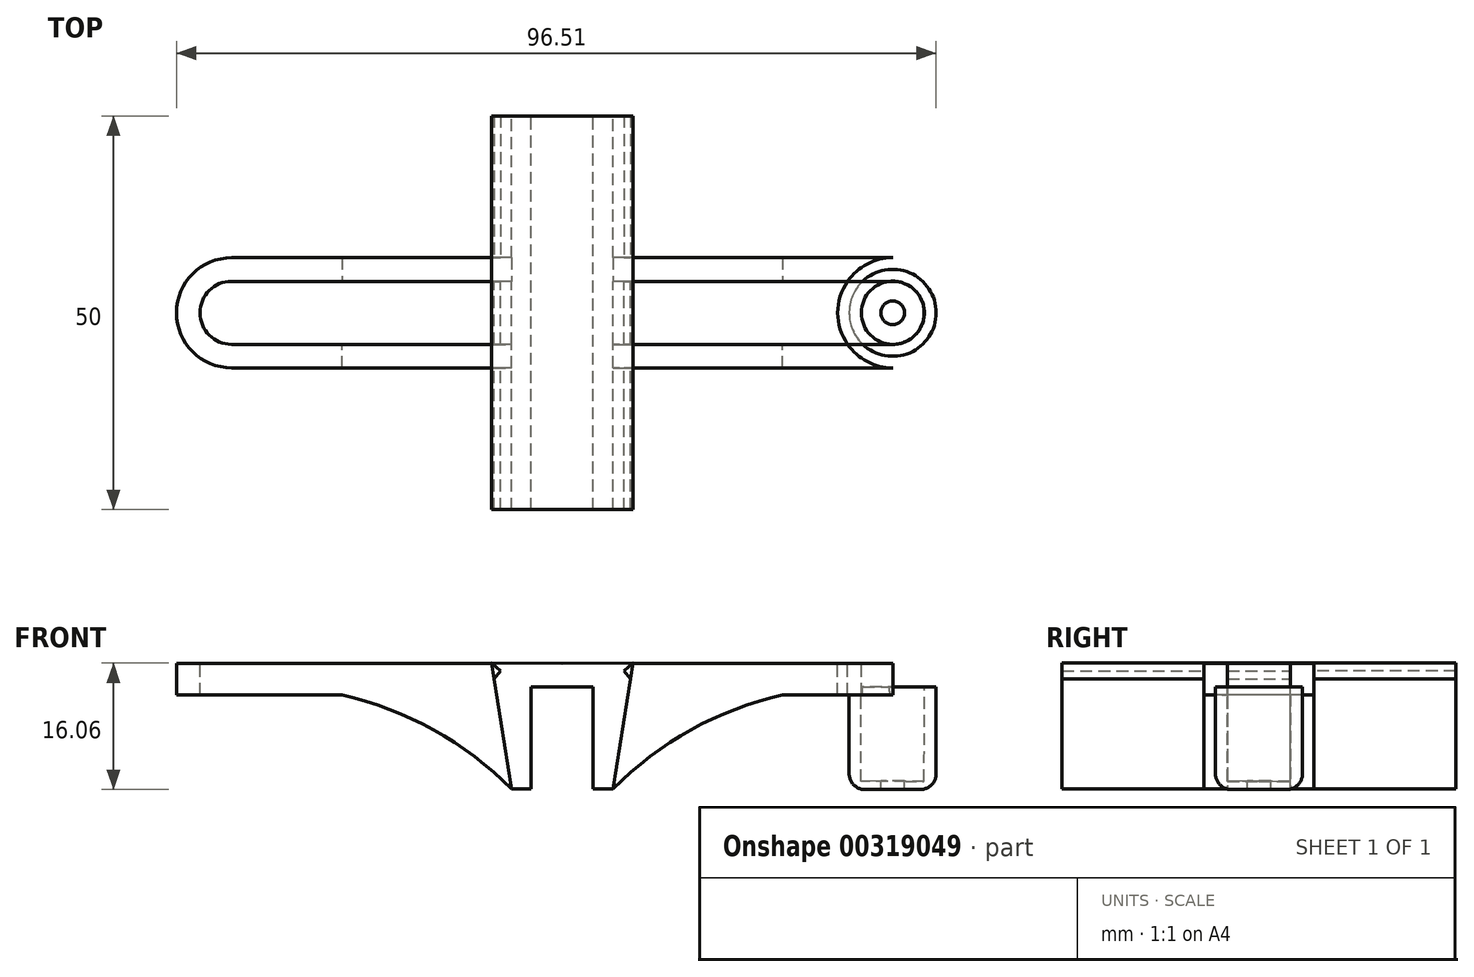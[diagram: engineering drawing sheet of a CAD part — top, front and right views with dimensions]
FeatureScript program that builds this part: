
annotation { "Feature Type Name" : "Feature", "Feature Type Description" : "" }
export const myFeature = defineFeature(function(context is Context, id is Id, definition is map)
    precondition{}
    {
        {
            var Q0;
            Q0=qCreatedBy(makeId("Front.planeOp"),FACE);
            var sketch = newSketch(context, id + "F0", { "sketchPlane" : qUnion([Q0])});
            skLineSegment(sketch, "E0", {"start": v(6.45, -15.97) * mm, "end": v(3.95, -15.97) * mm});
            skLineSegment(sketch, "E1", {"start": v(3.95, -15.97) * mm, "end": v(3.95, -2.97) * mm});
            skLineSegment(sketch, "E2", {"start": v(0, 0) * mm, "end": v(0, -15.97) * mm, "construction": true});
            skLineSegment(sketch, "E3", {"start": v(9, 0.03) * mm, "end": v(49, 0.03) * mm});
            skLineSegment(sketch, "E4", {"start": v(49, 0.03) * mm, "end": v(49, -2.97) * mm});
            skLineSegment(sketch, "E5", {"start": v(49, -2.97) * mm, "end": v(8.52, -2.97) * mm});
            skLineSegment(sketch, "E6", {"start": v(49, 0.03) * mm, "end": v(46, 0.03) * mm, "construction": true});
            skLineSegment(sketch, "E7", {"start": v(46, 0.03) * mm, "end": v(46, -2.97) * mm});
            skLineSegment(sketch, "E8", {"start": v(0, 0) * mm, "end": v(0, -2.97) * mm});
            skLineSegment(sketch, "E9", {"start": v(9, 0.03) * mm, "end": v(0, 0) * mm});
            skLineSegment(sketch, "E10", {"start": v(0, -2.97) * mm, "end": v(3.95, -2.97) * mm});
            skLineSegment(sketch, "E11", {"start": v(8.52, -2.97) * mm, "end": v(49, -2.97) * mm});
            skLineSegment(sketch, "E12.MirrorCS", {"start": v(0, -2.97) * mm, "end": v(-3.95, -2.97) * mm});
            skLineSegment(sketch, "E13.MirrorCS", {"start": v(-9, 0.03) * mm, "end": v(0, 0) * mm});
            skLineSegment(sketch, "E14.MirrorCS", {"start": v(-3.95, -15.97) * mm, "end": v(-3.95, -2.97) * mm});
            skLineSegment(sketch, "E15.MirrorCS", {"start": v(-6.45, -15.97) * mm, "end": v(-3.95, -15.97) * mm});
            skLineSegment(sketch, "E16.MirrorCS", {"start": v(-9, 0.03) * mm, "end": v(-49, 0.03) * mm});
            skLineSegment(sketch, "E17.MirrorCS", {"start": v(-49, 0.03) * mm, "end": v(-49, -2.97) * mm});
            skLineSegment(sketch, "E18.MirrorCS", {"start": v(-49, -2.97) * mm, "end": v(-8.52, -2.97) * mm});
            skLineSegment(sketch, "E19.MirrorCS", {"start": v(-46, 0.03) * mm, "end": v(-46, -2.97) * mm});
            skLineSegment(sketch, "E20", {"start": v(38, 0.03) * mm, "end": v(38, -2.97) * mm});
            skLineSegment(sketch, "E21", {"start": v(35, 0.03) * mm, "end": v(35, -2.97) * mm});
            skLineSegment(sketch, "E22", {"start": v(45.98, -14.97) * mm, "end": v(46, -2.97) * mm});
            skLineSegment(sketch, "E23", {"start": v(36.5, -2.97) * mm, "end": v(36.5, -16.03) * mm});
            skLineSegment(sketch, "E24", {"start": v(36.5, -16.03) * mm, "end": v(47.5, -16.03) * mm});
            skLineSegment(sketch, "E25", {"start": v(47.5, -16.03) * mm, "end": v(47.5, -2.97) * mm});
            skLineSegment(sketch, "E26", {"start": v(45.98, -14.97) * mm, "end": v(37.98, -14.96) * mm});
            skLineSegment(sketch, "E27", {"start": v(37.98, -14.96) * mm, "end": v(38, -2.97) * mm});
            skLineSegment(sketch, "E28", {"start": v(41.98, 0) * mm, "end": v(41.98, -16.03) * mm, "construction": true});
            skPoint(sketch, "E28.startSnap0", {"position": v(41.98, -14.96) * mm});
            skLineSegment(sketch, "E29", {"start": v(43.48, -14.97) * mm, "end": v(43.48, -16.03) * mm});
            skLineSegment(sketch, "E30", {"start": v(40.48, -14.96) * mm, "end": v(40.48, -16.03) * mm});
            skLineSegment(sketch, "E31", {"start": v(41.98, 0) * mm, "end": v(41.98, -16.03) * mm});
            skLineSegment(sketch, "E32", {"start": v(-8.52, -2.97) * mm, "end": v(-3.95, -2.97) * mm});
            skLineSegment(sketch, "E33", {"start": v(3.95, -2.97) * mm, "end": v(8.52, -2.97) * mm});
            skLineSegment(sketch, "E34", {"start": v(9, 0.03) * mm, "end": v(7.83, -0.97) * mm});
            skLineSegment(sketch, "E35", {"start": v(7.83, -0.97) * mm, "end": v(8.68, -1.97) * mm});
            skLineSegment(sketch, "E36.MirrorCS", {"start": v(-9, 0.03) * mm, "end": v(-7.83, -0.97) * mm});
            skLineSegment(sketch, "E37.MirrorCS", {"start": v(-7.83, -0.97) * mm, "end": v(-8.68, -1.97) * mm});
            skLineSegment(sketch, "E38", {"start": v(9, 0.03) * mm, "end": v(8.68, -1.97) * mm});
            skLineSegment(sketch, "E39", {"start": v(-9, 0.03) * mm, "end": v(-8.68, -1.97) * mm});
            skLineSegment(sketch, "E40", {"start": v(8.68, -1.97) * mm, "end": v(8.52, -2.97) * mm});
            skLineSegment(sketch, "E41", {"start": v(8.52, -2.97) * mm, "end": v(6.45, -15.97) * mm});
            skLineSegment(sketch, "E42", {"start": v(-8.68, -1.97) * mm, "end": v(-8.52, -2.97) * mm});
            skLineSegment(sketch, "E43", {"start": v(-8.52, -2.97) * mm, "end": v(-6.45, -15.97) * mm});
            skArc(sketch, "E44", {"start": v(35, -2.97) * mm, "mid": v(19.53, -6.85) * mm, "end": v(6.45, -15.97) * mm});
            skArc(sketch, "E45.MirrorCS", {"start": v(-35, -2.97) * mm, "mid": v(-19.53, -6.85) * mm, "end": v(-6.45, -15.97) * mm});
            skLineSegment(sketch, "E46", {"start": v(8.52, -2.97) * mm, "end": v(35, -2.97) * mm});
            skSolve(sketch);
        }
        {
            var Q0;
            Q0=qCreatedBy(makeId("Top.planeOp"),FACE);
            var sketch = newSketch(context, id + "F1", { "sketchPlane" : qUnion([Q0])});
            skLineSegment(sketch, "E47", {"start": v(0, 25) * mm, "end": v(0, -25) * mm, "construction": true});
            skLineSegment(sketch, "E48", {"start": v(0, 25) * mm, "end": v(9, 25) * mm});
            skLineSegment(sketch, "E49", {"start": v(0, -25) * mm, "end": v(9, -25) * mm});
            skLineSegment(sketch, "E50", {"start": v(0, 7) * mm, "end": v(9, 7) * mm, "construction": true});
            skLineSegment(sketch, "E51", {"start": v(9, 4) * mm, "end": v(0, 4) * mm, "construction": true});
            skLineSegment(sketch, "E52", {"start": v(0, -4) * mm, "end": v(9, -4) * mm, "construction": true});
            skLineSegment(sketch, "E53", {"start": v(9, -4) * mm, "end": v(9, -7) * mm, "construction": true});
            skLineSegment(sketch, "E54", {"start": v(9, -7) * mm, "end": v(0, -7) * mm, "construction": true});
            skLineSegment(sketch, "E55", {"start": v(9, 25) * mm, "end": v(9, 7) * mm});
            skLineSegment(sketch, "E56", {"start": v(9, -25) * mm, "end": v(9, -7) * mm});
            skLineSegment(sketch, "E57", {"start": v(0, 0) * mm, "end": v(0, 7) * mm, "construction": true});
            skLineSegment(sketch, "E58", {"start": v(0, 0) * mm, "end": v(0, -7) * mm, "construction": true});
            skPoint(sketch, "E59.endSnap0", {"position": v(4.5, -7) * mm});
            skLineSegment(sketch, "E60", {"start": v(49, 7) * mm, "end": v(49, -7) * mm, "construction": true});
            skPoint(sketch, "E61.endSnap0", {"position": v(4.5, 4) * mm});
            skLineSegment(sketch, "E62", {"start": v(49, 4) * mm, "end": v(49, -4) * mm, "construction": true});
            skPoint(sketch, "E62.endSnap0", {"position": v(4.5, -4) * mm});
            skLineSegment(sketch, "E63", {"start": v(42, 0) * mm, "end": v(42, -7) * mm, "construction": true});
            skLineSegment(sketch, "E64", {"start": v(42, 0) * mm, "end": v(42, 7) * mm, "construction": true});
            skArc(sketch, "E65", {"start": v(42, 7) * mm, "mid": v(49, 0) * mm, "end": v(42, -7) * mm});
            skArc(sketch, "E66", {"start": v(42, 4) * mm, "mid": v(46, 0) * mm, "end": v(42, -4) * mm});
            skLineSegment(sketch, "E67", {"start": v(46, 0) * mm, "end": v(46, 7) * mm, "construction": true});
            skLineSegment(sketch, "E68", {"start": v(46, 0) * mm, "end": v(46, -7) * mm, "construction": true});
            skLineSegment(sketch, "E69", {"start": v(0, 25) * mm, "end": v(0, -25) * mm});
            skLineSegment(sketch, "E70", {"start": v(9, 7) * mm, "end": v(7.5, 7) * mm, "construction": true});
            skLineSegment(sketch, "E71", {"start": v(7.5, 7) * mm, "end": v(7.5, -7) * mm, "construction": true});
            skLineSegment(sketch, "E72", {"start": v(7.5, 7) * mm, "end": v(42, 7) * mm});
            skLineSegment(sketch, "E73", {"start": v(7.5, 7) * mm, "end": v(7.5, 4) * mm});
            skLineSegment(sketch, "E74", {"start": v(7.5, 4) * mm, "end": v(42, 4) * mm});
            skLineSegment(sketch, "E75", {"start": v(42, -4) * mm, "end": v(7.5, -4) * mm});
            skLineSegment(sketch, "E76", {"start": v(7.5, -4) * mm, "end": v(7.5, -7) * mm});
            skLineSegment(sketch, "E77", {"start": v(42, -7) * mm, "end": v(7.5, -7) * mm});
            skLineSegment(sketch, "E78.MirrorCS", {"start": v(0, 25) * mm, "end": v(-9, 25) * mm});
            skLineSegment(sketch, "E79.MirrorCS", {"start": v(-9, 25) * mm, "end": v(-9, 7) * mm});
            skLineSegment(sketch, "E80.MirrorCS", {"start": v(-7.5, 7) * mm, "end": v(-42, 7) * mm});
            skArc(sketch, "E81.MirrorCS", {"start": v(-42, 7) * mm, "mid": v(-49, 0) * mm, "end": v(-42, -7) * mm});
            skArc(sketch, "E82.MirrorCS", {"start": v(-42, 4) * mm, "mid": v(-46, 0) * mm, "end": v(-42, -4) * mm});
            skLineSegment(sketch, "E83.MirrorCS", {"start": v(-7.5, 4) * mm, "end": v(-42, 4) * mm});
            skLineSegment(sketch, "E84.MirrorCS", {"start": v(-42, -7) * mm, "end": v(-7.5, -7) * mm});
            skLineSegment(sketch, "E85.MirrorCS", {"start": v(-42, -4) * mm, "end": v(-7.5, -4) * mm});
            skLineSegment(sketch, "E86.MirrorCS", {"start": v(-9, -25) * mm, "end": v(-9, -7) * mm});
            skLineSegment(sketch, "E87.MirrorCS", {"start": v(0, -25) * mm, "end": v(-9, -25) * mm});
            skLineSegment(sketch, "E88", {"start": v(-7.5, 4) * mm, "end": v(-7.5, 7) * mm});
            skLineSegment(sketch, "E89", {"start": v(-7.5, -4) * mm, "end": v(-7.5, -7) * mm});
            skLineSegment(sketch, "E90", {"start": v(-7.5, 7) * mm, "end": v(-7.5, 4) * mm});
            skLineSegment(sketch, "E91", {"start": v(-9, 7) * mm, "end": v(-9, -7) * mm, "construction": true});
            skLineSegment(sketch, "E92", {"start": v(-9, 4) * mm, "end": v(-9, -4) * mm});
            skLineSegment(sketch, "E93", {"start": v(9, 4) * mm, "end": v(9, -4) * mm});
            skLineSegment(sketch, "E94", {"start": v(9, 4) * mm, "end": v(7.5, 4) * mm});
            skArc(sketch, "E95", {"start": v(42, 4) * mm, "mid": v(38, 0) * mm, "end": v(42, -4) * mm});
            skArc(sketch, "E96", {"start": v(42, 7) * mm, "mid": v(35, 0) * mm, "end": v(42, -7) * mm});
            skLineSegment(sketch, "E97", {"start": v(38, 0) * mm, "end": v(38, 7) * mm, "construction": true});
            skLineSegment(sketch, "E98", {"start": v(38, 0) * mm, "end": v(38, -7) * mm, "construction": true});
            skLineSegment(sketch, "E99", {"start": v(35, 0) * mm, "end": v(35, 7) * mm, "construction": true});
            skLineSegment(sketch, "E100", {"start": v(35, 0) * mm, "end": v(35, -7) * mm, "construction": true});
            skSolve(sketch);
        }
        {
            var Q0;
            Q0=makeQuery(id+"F0.imprint","IMPRINT",FACE,{"disambiguationData":[TD([[makeQuery(id+"F0.imprint","IMPRINT",EDGE,{"derivedFrom":sQuery(id+"F0.wireOp",EDGE,"U2EiTiml-0wfB-zGtA-0Wzl-NFMzNxuxbPp0")}),-1.0]])]});
            var Q1;
            Q1=makeQuery(id+"F0.imprint","IMPRINT",FACE,{"disambiguationData":[TD([[makeQuery(id+"F0.imprint","IMPRINT",EDGE,{"derivedFrom":sQuery(id+"F0.wireOp",EDGE,"E8")}),-1.0]])]});
            var Q2;
            Q2=makeQuery(id+"F0.imprint","IMPRINT",FACE,{"disambiguationData":[TD([[makeQuery(id+"F0.imprint","IMPRINT",EDGE,{"derivedFrom":sQuery(id+"F0.wireOp",EDGE,"E8")}),1.0]])]});
            var Q3;
            Q3=makeQuery(id+"F0.imprint","IMPRINT",FACE,{"disambiguationData":[TD([[makeQuery(id+"F0.imprint","IMPRINT",EDGE,{"derivedFrom":sQuery(id+"F0.wireOp",EDGE,"E14.MirrorCS")}),1.0]])]});
            var Q4;
            Q4=makeQuery(id+"F0.imprint","IMPRINT",FACE,{"disambiguationData":[TD([[makeQuery(id+"F0.imprint","IMPRINT",EDGE,{"derivedFrom":sQuery(id+"F0.wireOp",EDGE,"E0")}),-1.0]])]});
            extrude(context, id + "F2", {"entities" : qUnion([Q0, Q1, Q2, Q3, Q4]), "endBound" : BoundingType.SYMMETRIC, "depth" : 50 * mm});
        }
        {
            var Q0;
            Q0=makeQuery(id+"F1.imprint","IMPRINT",FACE,{"disambiguationData":[TD([[makeQuery(id+"F1.imprint","IMPRINT",EDGE,{"derivedFrom":sQuery(id+"F1.wireOp",EDGE,"E65")}),-1.0]])]});
            var Q1;
            {var subQ5=sQuery(id+"F1.wireOp",EDGE,"E76");Q1=makeQuery(id+"F1.imprint","IMPRINT",FACE,{"disambiguationData":[TD([[makeQuery(id+"F1.imprint","IMPRINT",EDGE,{"derivedFrom":subQ5}),1.0]])]});}
            var Q2;
            {var subQ5=sQuery(id+"F1.wireOp",EDGE,"E73");Q2=makeQuery(id+"F1.imprint","IMPRINT",FACE,{"disambiguationData":[TD([[makeQuery(id+"F1.imprint","IMPRINT",EDGE,{"derivedFrom":subQ5}),1.0]])]});}
            var Q3;
            {var subQ0=sQuery(id+"F1.wireOp",EDGE,"E89");Q3=makeQuery(id+"F1.imprint","IMPRINT",FACE,{"disambiguationData":[TD([[makeQuery(id+"F1.imprint","IMPRINT",EDGE,{"derivedFrom":subQ0}),-1.0]])]});}
            var Q4;
            {var subQ0=sQuery(id+"F1.wireOp",EDGE,"E95");Q4=makeQuery(id+"F1.imprint","IMPRINT",FACE,{"disambiguationData":[TD([[makeQuery(id+"F1.imprint","IMPRINT",EDGE,{"derivedFrom":subQ0}),-1.0]])]});}
            extrude(context, id + "F3", {"entities" : qUnion([Q0, Q1, Q2, Q3, Q4]), "depth" : -4 * mm});
        }
        {
            var Q0;
            {var subQ1=sQuery(id+"F0.wireOp",EDGE,"E22");Q0=makeQuery(id+"F0.imprint","IMPRINT",FACE,{"disambiguationData":[TD([[makeQuery(id+"F0.imprint","IMPRINT",EDGE,{"derivedFrom":subQ1}),-1.0]])]});}
            var Q1;
            Q1=sQuery(id+"F0.wireOp",EDGE,"E31");
            revolve(context, id + "F4", {"operationType" : NewBodyOperationType.ADD, "entities" : qUnion([Q0]), "axis" : qUnion([Q1]), "revolveType" : RevolveType.FULL});
        }
        {
            var Q0;
            Q0=makeQuery(id+"F4.opRevolve","SWEPT_EDGE",EDGE,{"disambiguationData":[OSD([sQuery(id+"F0.wireOp",EDGE,"E24"),sQuery(id+"F0.wireOp",EDGE,"E25")])]});
            fillet(context, id + "F5", {"entities" : qUnion([Q0]), "radius" : 2 * mm, "tangentPropagation" : true, "allowEdgeOverflow" : false});
        }
        {
            var Q0;
            Q0=makeQuery(id+"F0.imprint","IMPRINT",FACE,{"disambiguationData":[TD([[makeQuery(id+"F0.imprint","IMPRINT",EDGE,{"derivedFrom":sQuery(id+"F0.wireOp",EDGE,"E34")}),1.0]])]});
            extrude(context, id + "F6", {"entities" : qUnion([Q0]), "depth" : 18 * mm});
        }
        {
            var Q0;
            Q0=makeQuery(id+"F6.opExtrude","SWEPT_BODY",BODY,{"disambiguationData":[OSD([sQuery(id+"F0.wireOp",EDGE,"E34"),sQuery(id+"F0.wireOp",EDGE,"E35"),sQuery(id+"F0.wireOp",EDGE,"E38")])]});
            transform(context, id + "F7", {"entities" : qUnion([Q0]), "transformType" : TransformType.TRANSLATION_3D, "dx" : 0 * mm, "dy" : -7 * mm, "dz" : 0 * mm, "makeCopy" : false});
        }
        {
            var Q0;
            Q0=makeQuery(id+"F6.opExtrude","SWEPT_BODY",BODY,{"disambiguationData":[OSD([sQuery(id+"F0.wireOp",EDGE,"E34"),sQuery(id+"F0.wireOp",EDGE,"E35"),sQuery(id+"F0.wireOp",EDGE,"E38")])]});
            var Q1;
            Q1=qCreatedBy(makeId("Front.planeOp"),FACE);
            mirror(context, id + "F8", {"entities" : qUnion([Q0]), "mirrorPlane" : qUnion([Q1])});
        }
        {
            var Q0;
            Q0=makeQuery(id+"F6.opExtrude","SWEPT_BODY",BODY,{"disambiguationData":[OSD([sQuery(id+"F0.wireOp",EDGE,"E34"),sQuery(id+"F0.wireOp",EDGE,"E35"),sQuery(id+"F0.wireOp",EDGE,"E38")])]});
            var Q1;
            Q1=makeQuery(id+"F8.opPattern","COPY",BODY,{"derivedFrom":makeQuery(id+"F6.opExtrude","SWEPT_BODY",BODY,{"disambiguationData":[OSD([sQuery(id+"F0.wireOp",EDGE,"E34"),sQuery(id+"F0.wireOp",EDGE,"E35"),sQuery(id+"F0.wireOp",EDGE,"E38")])]}),"instanceName":"1"});
            var Q2;
            Q2=qCreatedBy(makeId("Right.planeOp"),FACE);
            mirror(context, id + "F9", {"entities" : qUnion([Q0, Q1]), "mirrorPlane" : qUnion([Q2])});
        }
        {
            var Q0;
            Q0=makeQuery(id+"F0.imprint","IMPRINT",FACE,{"disambiguationData":[TD([[makeQuery(id+"F0.imprint","IMPRINT",EDGE,{"derivedFrom":sQuery(id+"F0.wireOp",EDGE,"E41")}),1.0]])]});
            extrude(context, id + "F10", {"entities" : qUnion([Q0]), "depth" : 3 * mm});
        }
        {
            var Q0;
            Q0=makeQuery(id+"F10.opExtrude","SWEPT_BODY",BODY,{"disambiguationData":[OSD([sQuery(id+"F0.wireOp",EDGE,"E41"),sQuery(id+"F0.wireOp",EDGE,"E44"),sQuery(id+"F0.wireOp",EDGE,"E46")])]});
            transform(context, id + "F11", {"entities" : qUnion([Q0]), "transformType" : TransformType.TRANSLATION_3D, "dx" : 0 * mm, "dy" : -4 * mm, "dz" : 0 * mm, "makeCopy" : false});
        }
        {
            var Q0;
            Q0=makeQuery(id+"F10.opExtrude","SWEPT_BODY",BODY,{"disambiguationData":[OSD([sQuery(id+"F0.wireOp",EDGE,"E41"),sQuery(id+"F0.wireOp",EDGE,"E44"),sQuery(id+"F0.wireOp",EDGE,"E46")])]});
            var Q1;
            Q1=qCreatedBy(makeId("Front.planeOp"),FACE);
            mirror(context, id + "F12", {"operationType" : NewBodyOperationType.ADD, "entities" : qUnion([Q0]), "mirrorPlane" : qUnion([Q1])});
        }
        {
            var Q0;
            {var subQ0=sQuery(id+"F0.wireOp",EDGE,"E43");Q0=makeQuery(id+"F0.imprint","IMPRINT",FACE,{"disambiguationData":[TD([[makeQuery(id+"F0.imprint","IMPRINT",EDGE,{"derivedFrom":subQ0}),-1.0]])]});}
            extrude(context, id + "F13", {"entities" : qUnion([Q0]), "depth" : 3 * mm});
        }
        {
            var Q0;
            Q0=makeQuery(id+"F13.opExtrude","SWEPT_BODY",BODY,{"disambiguationData":[OSD([sQuery(id+"F0.wireOp",EDGE,"E18.MirrorCS"),sQuery(id+"F0.wireOp",EDGE,"E43"),sQuery(id+"F0.wireOp",EDGE,"E45.MirrorCS")])]});
            transform(context, id + "F14", {"entities" : qUnion([Q0]), "transformType" : TransformType.TRANSLATION_3D, "dx" : 0 * mm, "dy" : -4 * mm, "dz" : 0 * mm, "makeCopy" : false});
        }
        {
            var Q0;
            Q0=makeQuery(id+"F13.opExtrude","SWEPT_BODY",BODY,{"disambiguationData":[OSD([sQuery(id+"F0.wireOp",EDGE,"E18.MirrorCS"),sQuery(id+"F0.wireOp",EDGE,"E43"),sQuery(id+"F0.wireOp",EDGE,"E45.MirrorCS")])]});
            var Q1;
            Q1=qCreatedBy(makeId("Front.planeOp"),FACE);
            mirror(context, id + "F15", {"operationType" : NewBodyOperationType.ADD, "entities" : qUnion([Q0]), "mirrorPlane" : qUnion([Q1])});
        }
    });
